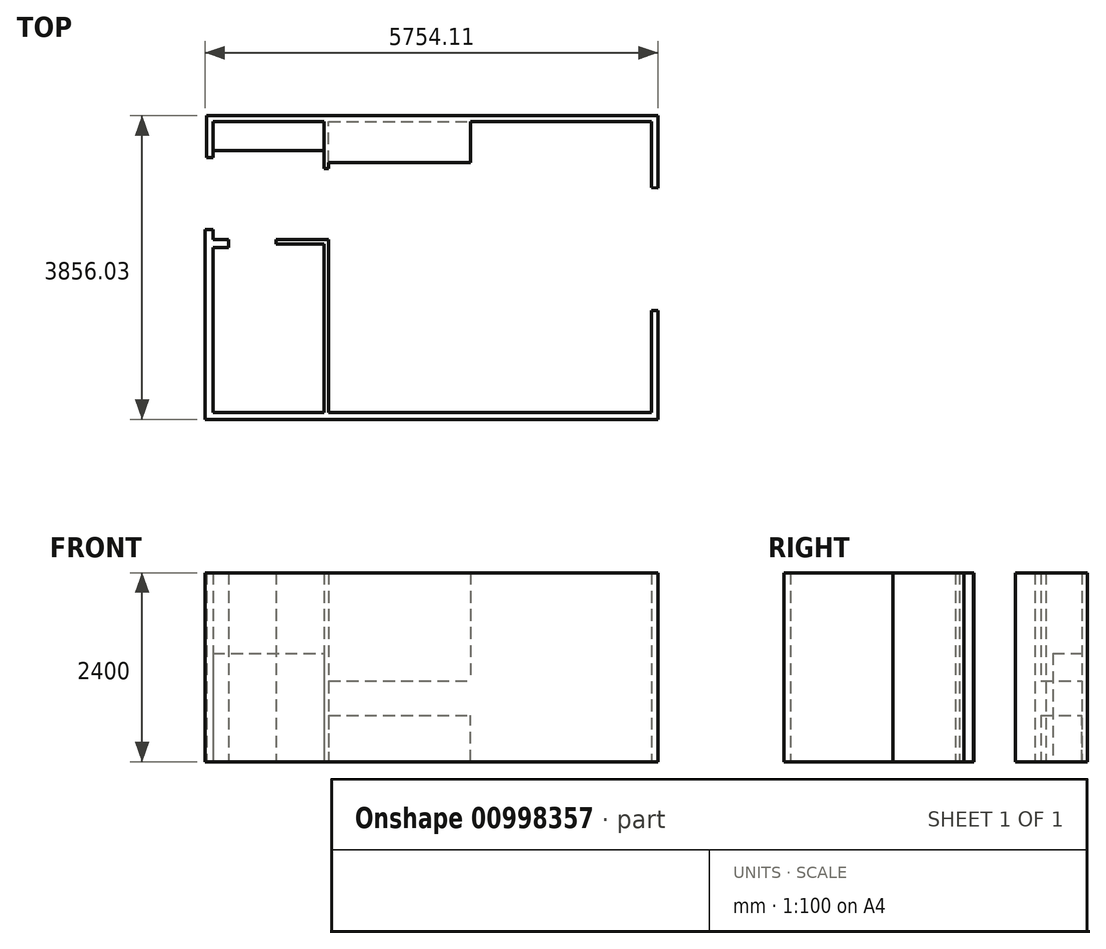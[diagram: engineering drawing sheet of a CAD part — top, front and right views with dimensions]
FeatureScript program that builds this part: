
annotation { "Feature Type Name" : "Feature", "Feature Type Description" : "" }
export const myFeature = defineFeature(function(context is Context, id is Id, definition is map)
    precondition{}
    {
        {
            var Q0;
            Q0=qCreatedBy(makeId("Top.planeOp"),FACE);
            var sketch = newSketch(context, id + "F0", { "sketchPlane" : qUnion([Q0])});
            skLineSegment(sketch, "E0", {"start": v(0, 0) * mm, "end": v(4100, 0) * mm});
            skLineSegment(sketch, "E1", {"start": v(4100, 0) * mm, "end": v(4100, 1300) * mm});
            skLineSegment(sketch, "E2", {"start": v(4100, 2860) * mm, "end": v(4100, 3700) * mm});
            skLineSegment(sketch, "E3", {"start": v(4100, 3700) * mm, "end": v(1800, 3700) * mm});
            skLineSegment(sketch, "E4", {"start": v(0, 0) * mm, "end": v(0, 2200) * mm});
            skLineSegment(sketch, "E5", {"start": v(1800, 3700) * mm, "end": v(0, 3700) * mm});
            skLineSegment(sketch, "E6", {"start": v(0, 3700) * mm, "end": v(0, 3100) * mm});
            skLineSegment(sketch, "E7", {"start": v(0, 2200) * mm, "end": v(-670, 2200) * mm});
            skLineSegment(sketch, "E8", {"start": v(-1270, 2200) * mm, "end": v(-1470, 2200) * mm});
            skLineSegment(sketch, "E9", {"start": v(0, 0) * mm, "end": v(-1470, 0) * mm});
            skLineSegment(sketch, "E10", {"start": v(-1470, 0) * mm, "end": v(-1470, 2200) * mm});
            skLineSegment(sketch, "E11", {"start": v(0, 3700) * mm, "end": v(-1470, 3700) * mm});
            skLineSegment(sketch, "E12", {"start": v(-1470, 2200) * mm, "end": v(-1470, 2324.14) * mm});
            skLineSegment(sketch, "E13", {"start": v(-1470, 3700) * mm, "end": v(-1470, 3240.48) * mm});
            skLineSegment(sketch, "E14", {"start": v(-1470, 3240.48) * mm, "end": v(-1552.38, 3240.48) * mm});
            skLineSegment(sketch, "E15", {"start": v(-1552.38, 3240.48) * mm, "end": v(-1552.38, 3771.48) * mm});
            skLineSegment(sketch, "E16", {"start": v(-1552.38, 3771.48) * mm, "end": v(4183.76, 3771.48) * mm});
            skLineSegment(sketch, "E17", {"start": v(4183.76, 3771.48) * mm, "end": v(4183.76, 2855.37) * mm});
            skLineSegment(sketch, "E18", {"start": v(4183.76, 2855.37) * mm, "end": v(4100, 2860) * mm});
            skLineSegment(sketch, "E19", {"start": v(4100, 1300) * mm, "end": v(4183.76, 1300) * mm});
            skLineSegment(sketch, "E20", {"start": v(4183.76, 1300) * mm, "end": v(4183.76, -84.55) * mm});
            skLineSegment(sketch, "E21", {"start": v(4183.76, -84.55) * mm, "end": v(-1570.35, -84.55) * mm});
            skLineSegment(sketch, "E22", {"start": v(-1570.35, -84.55) * mm, "end": v(-1570.35, 2328.46) * mm});
            skLineSegment(sketch, "E23", {"start": v(-1570.35, 2328.46) * mm, "end": v(-1470, 2324.14) * mm});
            skLineSegment(sketch, "E24", {"start": v(0, 3700) * mm, "end": v(-61.47, 3700) * mm});
            skLineSegment(sketch, "E25", {"start": v(-61.47, 3700) * mm, "end": v(-61.47, 3100) * mm});
            skLineSegment(sketch, "E26", {"start": v(-61.47, 3100) * mm, "end": v(0, 3100) * mm});
            skLineSegment(sketch, "E27", {"start": v(-670, 2200) * mm, "end": v(-670, 2142.85) * mm});
            skLineSegment(sketch, "E28", {"start": v(-670, 2142.85) * mm, "end": v(-61.47, 2142.85) * mm});
            skLineSegment(sketch, "E29", {"start": v(-61.47, 2142.85) * mm, "end": v(-61.47, 0) * mm});
            skLineSegment(sketch, "E30", {"start": v(-1270, 2200) * mm, "end": v(-1270, 2094.73) * mm});
            skLineSegment(sketch, "E31", {"start": v(-1270, 2094.73) * mm, "end": v(-1470, 2094.73) * mm});
            skSolve(sketch);
        }
        {
            var Q0;
            Q0 = qSketchRegion(id + "F0", true);
            extrude(context, id + "F1", {"entities" : qUnion([Q0]), "depth" : 2400 * mm, "offsetDistance" : 25 * mm});
        }
        {
            var Q0;
            Q0=makeQuery(id+"F1.opExtrude","SWEPT_FACE",FACE,{"disambiguationData":[OSD([sQuery(id+"F0.wireOp",EDGE,"E3"),sQuery(id+"F0.wireOp",EDGE,"E5")])]});
            var sketch = newSketch(context, id + "F2", { "sketchPlane" : qUnion([Q0])});
            skLineSegment(sketch, "E32.bottom", {"start": v(0, 0) * mm, "end": v(1800, 0) * mm});
            skLineSegment(sketch, "E32.top", {"start": v(0, 588.13) * mm, "end": v(1800, 588.13) * mm});
            skLineSegment(sketch, "E32.left", {"start": v(0, 0) * mm, "end": v(0, 588.13) * mm});
            skLineSegment(sketch, "E32.right", {"start": v(1800, 0) * mm, "end": v(1800, 588.13) * mm});
            skLineSegment(sketch, "E33.bottom", {"start": v(0, 2400) * mm, "end": v(1800, 2400) * mm});
            skLineSegment(sketch, "E33.top", {"start": v(0, 1023.7) * mm, "end": v(1800, 1023.7) * mm});
            skLineSegment(sketch, "E33.left", {"start": v(0, 2400) * mm, "end": v(0, 1023.7) * mm});
            skLineSegment(sketch, "E33.right", {"start": v(1800, 2400) * mm, "end": v(1800, 1023.7) * mm});
            skSolve(sketch);
        }
        {
            var Q0;
            Q0 = qSketchRegion(id + "F2", true);
            extrude(context, id + "F3", {"entities" : qUnion([Q0]), "operationType" : NewBodyOperationType.ADD, "depth" : 520 * mm, "offsetDistance" : 25 * mm});
        }
        {
            var Q0;
            Q0=makeQuery(id+"F1.opExtrude","SWEPT_FACE",FACE,{"disambiguationData":[OSD([sQuery(id+"F0.wireOp",EDGE,"E11")])]});
            var sketch = newSketch(context, id + "F4", { "sketchPlane" : qUnion([Q0])});
            skLineSegment(sketch, "E34.bottom", {"start": v(-1470, 0) * mm, "end": v(-61.47, 0) * mm});
            skLineSegment(sketch, "E34.top", {"start": v(-1470, 1377.9) * mm, "end": v(-61.47, 1377.9) * mm});
            skLineSegment(sketch, "E34.left", {"start": v(-1470, 0) * mm, "end": v(-1470, 1377.9) * mm});
            skLineSegment(sketch, "E34.right", {"start": v(-61.47, 0) * mm, "end": v(-61.47, 1377.9) * mm});
            skSolve(sketch);
        }
        {
            var Q0;
            Q0=makeQuery(id+"F4.imprint","IMPRINT",FACE,{"disambiguationData":[TD([[makeQuery(id+"F4.imprint","IMPRINT",EDGE,{"derivedFrom":sQuery(id+"F4.wireOp",EDGE,"E34.bottom")}),-1.0]])]});
            extrude(context, id + "F5", {"entities" : qUnion([Q0]), "operationType" : NewBodyOperationType.ADD, "depth" : 370 * mm, "offsetDistance" : 25 * mm});
        }
    });
